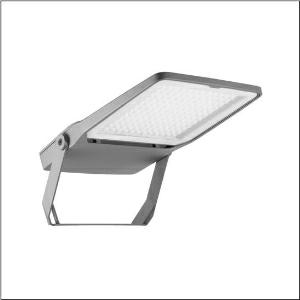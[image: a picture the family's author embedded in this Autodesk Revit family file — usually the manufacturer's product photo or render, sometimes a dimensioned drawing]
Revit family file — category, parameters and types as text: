
# Revit family: floodlight_fl_20_midi___pl43_5xa7682d3a1ac_4fa5
name_source: partatom
category: Lighting Fixtures
units: mm (PartAtom-declared; Revit-internal decimal feet)

## family parameters
Cut with Voids When Loaded = No
Host = Face
Light Source = No
Part Type = Normal
Room Calculation Point = No
Round Connector Dimension = Use Diameter
Shared = No

## types (1)
- --- (1 x LED 5000K / CRI = 70 (unbekannt), 19360 lm, 5000K)
    Apparent Load = 142 VA
    CIE Flux Codes = 32 74 99 100 100
    Color Rendering = 70
    Color Temperature = 5000K
    Default Elevation = 1800 mm
    Description = Floodlight FL 20 midi, floodlight, primary light control with lens, of plastic, primary optical cover: protective disc, of toughened safety glass, transparent, light distribution: PL43, light emission: direct distribution, primary light characteristic: asymmetric, installation type: surface-mounted, LED, High Power LED, rated luminous flux: 19.360lm, luminous efficacy: 136lm/W, light colour: 750, colour temperature: 5000K, control gear: ECG Plus, control: flexible luminous flux parameterisation, time-dependent luminous flux control, digital communication interface, power reduction, overheat protection, electronic power reduction, with terminal, 5-pole, max. 2.5mm², mains connection: 220..240V, AC, 50/60Hz, rated input power: 142W, LED unit, of diecast aluminium, powder-coated, Siteco® metallic grey (DB 702S), corrosivity category C5 mid according to DIN EN ISO 12944, incl. 1x M20 cable gland for cable Ø 6.5..12mm, length: 654mm, width: 450mm, height: 76mm, housing frame, of diecast aluminium, powder-coated, Siteco® metallic grey (DB 702S), mounting bracket, of steel, powder-coated, Siteco® metallic grey (DB 702S), DALI, protection rating (complete): IP66, insulation class (complete): insulation class II (safety insulation), certification: CE, ENEC, VDE, protection symbol: D, permissible operating ambient temperature: -40..+40°C, permissible operating ambient temperature for outdoor applications: -40..+50°C, standard: DIN EN 12944, packaging unit: 1 piece

Light Distribution: PL43
    Height = 76 mm
    Lamp = 1 x LED 5000K / CRI >= 70 (unbekannt)
    Lamp Light Flux = 19360 lm
    Lamp count = 1
    Length = 672 mm
    Luminous efficacy = 136 lm/W
    Manufacturer = Siteco
    ModVariant = No
    Model = 5XA7682D3A1AC
    Mounting Place = Wall
    Mounting Type = Surface mounted
    Number of Poles = 1
    OnlyDefault = Yes
    Power Factor = 1
    Product Name = Floodlight FL 20 midi | PL43
    Product group = floodlight | wall mounted
    ProductGroupID = 2001
    Protection Class = Protection class II
    Protection Degree = IP 66
    RLX_Detail_Level = 1
    RLX_Emergency_Light_Flux = 0 lm
    RLX_Emergency_Type = 0
    RLX_Emergency_Type_DB = No
    RlxData = <blob elided: 97497 chars, md5=838fa763>
    Socket = socket
    Standby Power = 0 W
    System Light Flux = 19360 lm
    System Power = 142 W
    Type Comments = factory setting: luminous flux: 100 % | dim-lin: 254 | 489 mA
    Type Image = l_1005943.jpg
    URL = http://relux.com
    VarID = @adj_148547
    Voltage = 0 V
    Weight = 0.00 kg
    Width = 450 mm

## geometry (parser evidence)
native form markers: Blend x4, Sweep x14
no freeform markers — native parametric forms only
